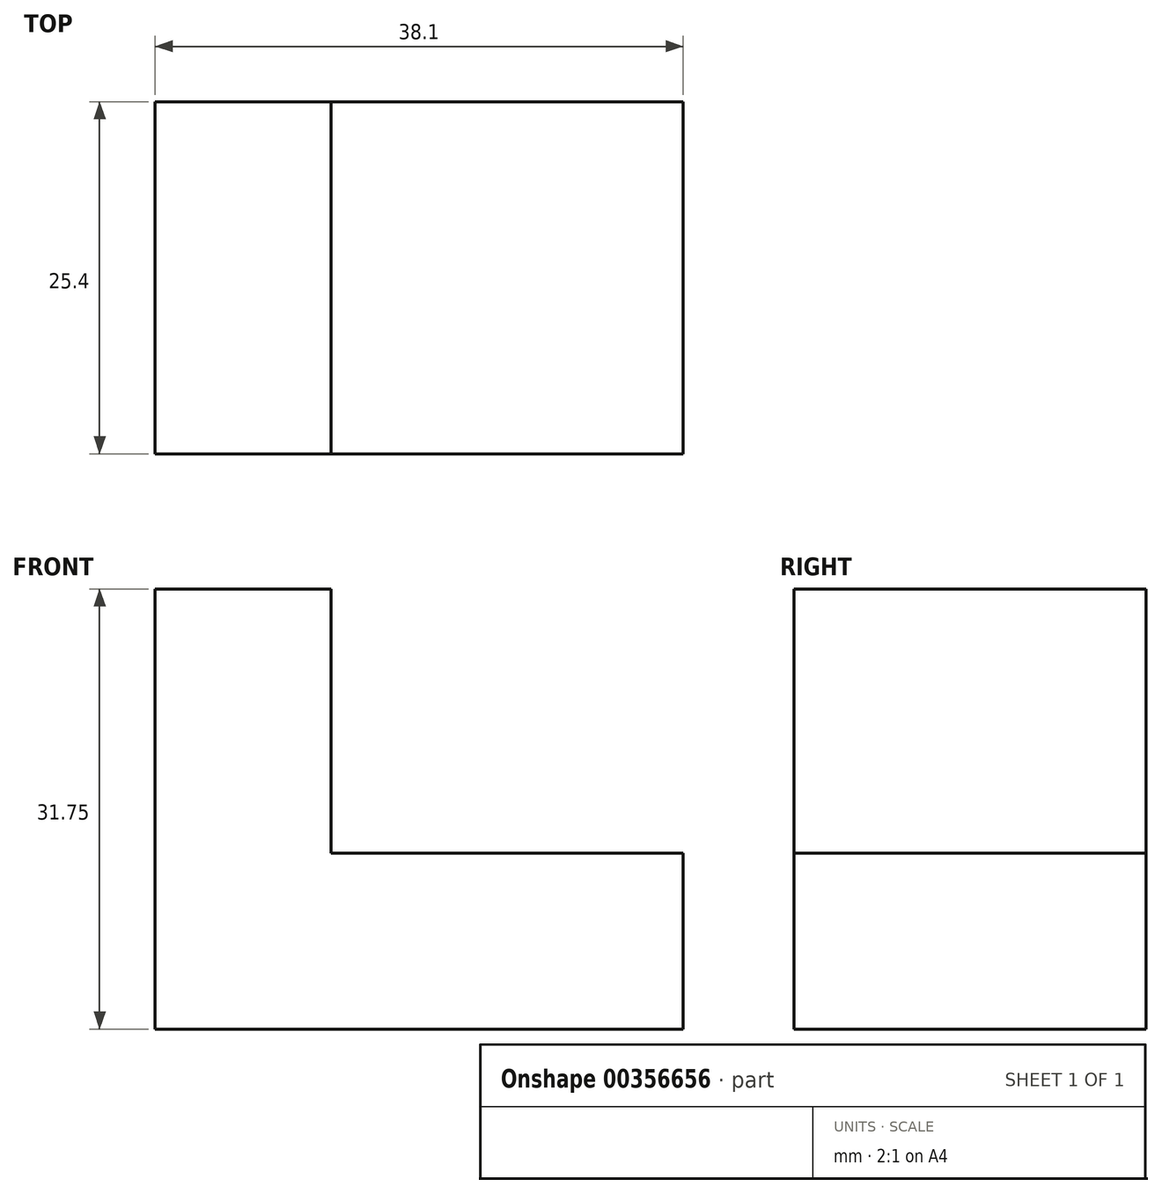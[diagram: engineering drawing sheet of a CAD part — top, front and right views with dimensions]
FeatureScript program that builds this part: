
annotation { "Feature Type Name" : "Feature", "Feature Type Description" : "" }
export const myFeature = defineFeature(function(context is Context, id is Id, definition is map)
    precondition{}
    {
        {
            var Q0;
            Q0=qCreatedBy(makeId("Front.planeOp"),FACE);
            var sketch = newSketch(context, id + "F0", { "sketchPlane" : qUnion([Q0])});
            skLineSegment(sketch, "E0", {"start": v(-31.99, 19.14) * mm, "end": v(-19.29, 19.14) * mm});
            skLineSegment(sketch, "E1", {"start": v(-19.29, 19.14) * mm, "end": v(-19.29, 0.09) * mm});
            skLineSegment(sketch, "E2", {"start": v(-19.29, 0.09) * mm, "end": v(6.11, 0.09) * mm});
            skLineSegment(sketch, "E3", {"start": v(6.11, 0.09) * mm, "end": v(6.11, -12.61) * mm});
            skLineSegment(sketch, "E4", {"start": v(6.11, -12.61) * mm, "end": v(-31.99, -12.61) * mm});
            skLineSegment(sketch, "E5", {"start": v(-31.99, -12.61) * mm, "end": v(-31.99, 19.14) * mm});
            skSolve(sketch);
        }
        {
            var Q0;
            Q0=makeQuery(id+"F0.imprint","IMPRINT",FACE,{"disambiguationData":[TD([[makeQuery(id+"F0.imprint","IMPRINT",EDGE,{"derivedFrom":sQuery(id+"F0.wireOp",EDGE,"E0")}),-1.0]])]});
            extrude(context, id + "F1", {"entities" : qUnion([Q0]), "depth" : 25.4 * mm});
        }
    });
